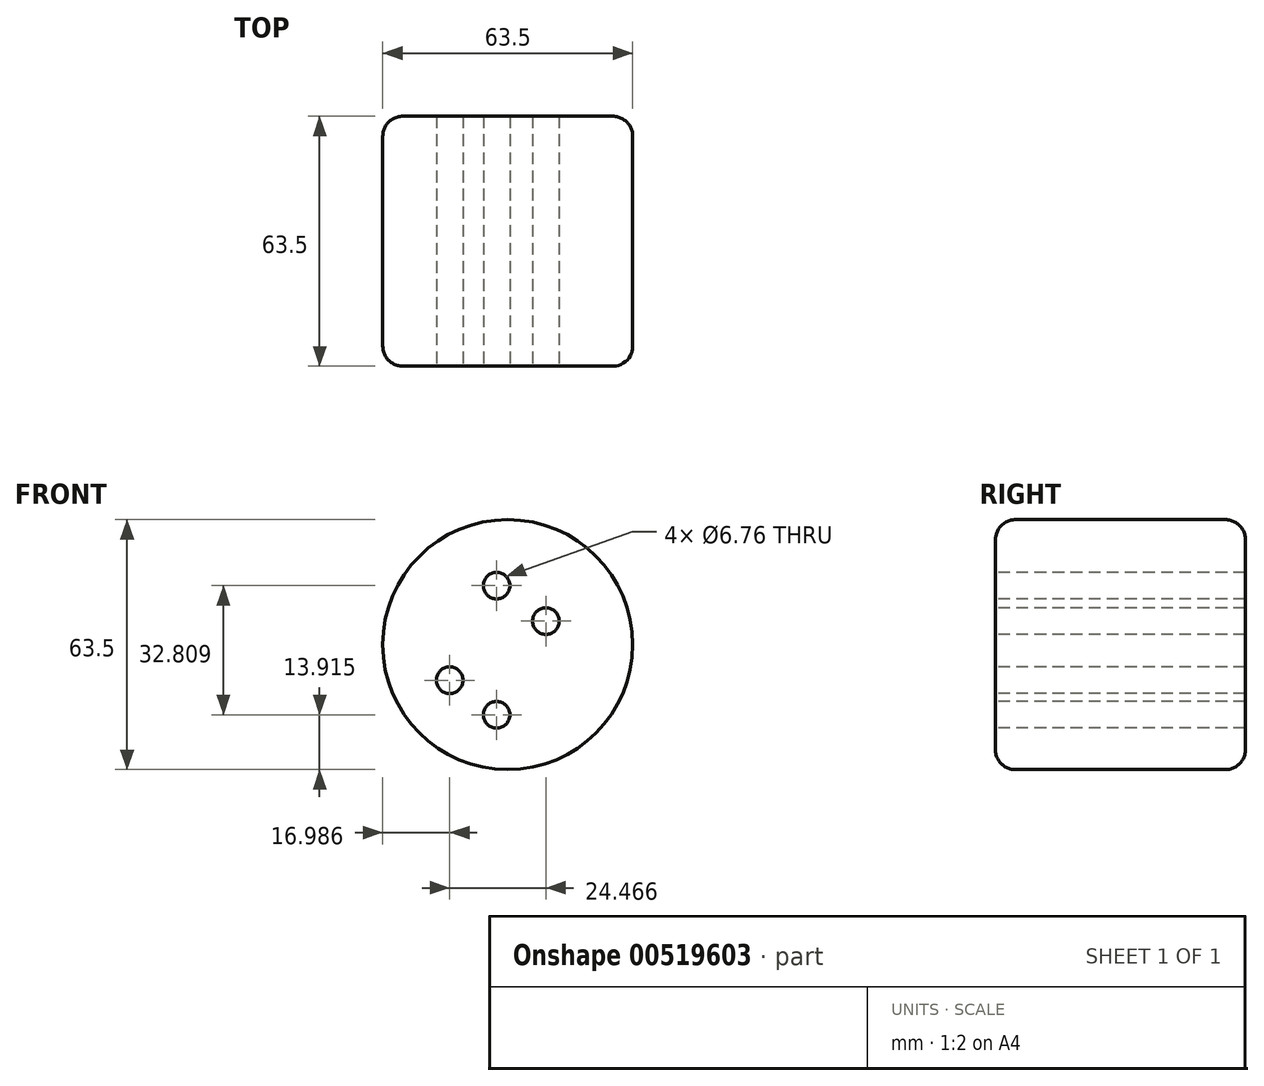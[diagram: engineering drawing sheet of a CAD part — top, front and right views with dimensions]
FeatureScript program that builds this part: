
annotation { "Feature Type Name" : "Feature", "Feature Type Description" : "" }
export const myFeature = defineFeature(function(context is Context, id is Id, definition is map)
    precondition{}
    {
        {
            var Q0;
            Q0=qCreatedBy(makeId("Front.planeOp"),FACE);
            var sketch = newSketch(context, id + "F0", { "sketchPlane" : qUnion([Q0])});
            skCircle(sketch, "E0", {"center": v(-34.22, 0) * mm, "radius": 31.75 * mm});
            skSolve(sketch);
        }
        {
            var Q0;
            Q0=makeQuery(id+"F0.imprint","IMPRINT",FACE,{"disambiguationData":[TD([[makeQuery(id+"F0.imprint","IMPRINT",EDGE,{"derivedFrom":sQuery(id+"F0.wireOp",EDGE,"E0")}),1.0]])]});
            extrude(context, id + "F1", {"entities" : qUnion([Q0]), "depth" : 63.5 * mm, "offsetDistance" : 25.4 * mm});
        }
        {
            var Q0;
            Q0=makeQuery(id+"F1.opExtrude","SWEPT_FACE",FACE,{"disambiguationData":[OSD([sQuery(id+"F0.wireOp",EDGE,"E0")])]});
            fillet(context, id + "F2", {"entities" : qUnion([Q0]), "radius" : 5.08 * mm, "tangentPropagation" : true, "allowEdgeOverflow" : false});
        }
        {
            var Q0;
            Q0=makeQuery(id+"F1.opExtrude","CAP_FACE",FACE,{"disambiguationData":[OSD([sQuery(id+"F0.wireOp",EDGE,"E0")])],"isStart":false});
            var sketch = newSketch(context, id + "F3", { "sketchPlane" : qUnion([Q0])});
            skPoint(sketch, "E1", {"position": v(-37.06, 14.97) * mm});
            skPoint(sketch, "E2", {"position": v(-37.06, -17.84) * mm});
            skPoint(sketch, "E3", {"position": v(-24.52, 5.98) * mm});
            skPoint(sketch, "E4", {"position": v(-48.98, -9.05) * mm});
            skSolve(sketch);
        }
        {
            var Q0;
            Q0=sQuery(id+"F3.wireOp",VERTEX,"E3");
            var Q1;
            Q1=sQuery(id+"F3.wireOp",VERTEX,"E1");
            var Q2;
            Q2=sQuery(id+"F3.wireOp",VERTEX,"E4");
            var Q3;
            Q3=sQuery(id+"F3.wireOp",VERTEX,"E2");
            var Q4;
            Q4=makeQuery(id+"F1.opExtrude","SWEPT_BODY",BODY,{"disambiguationData":[OSD([sQuery(id+"F0.wireOp",EDGE,"E0")])]});
            hole(context, id + "F4", {"style" : HoleStyle.SIMPLE, "endStyle" : HoleEndStyle.THROUGH, "standardTappedOrClearance" : lookupTablePath({ "standard" : "ANSI", "fit" : "Normal (ASME)", "size" : "1/4", "type" : "Clearance" }), "standardBlindInLast" : lookupTablePath({ "fit" : "Free", "standard" : "ANSI", "size" : "1/4", "type" : "Clearance" }), "holeDiameter" : 6.76 * mm, "isTappedThrough" : true, "tappedDepth" : 12.7 * mm, "tapClearance" : 3, "locations" : qUnion([Q0, Q1, Q2, Q3]), "scope" : qUnion([Q4])});
        }
    });
